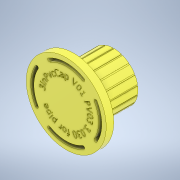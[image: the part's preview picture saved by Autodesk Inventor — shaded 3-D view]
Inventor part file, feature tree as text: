
AUTODESK INVENTOR PART (.ipt)
format: ipt  version: 2022.2 (Build 262287000, 287)  size: 949,760 bytes
history: native  units: in
note: dims shown in document units (in); Inventor stores cm internally (conversion verified against a paired STEP export)
features: extrude x6, sketch x6, pattern_circular x2, emboss x1
ambient origin geometry x8: Origin, YZ Plane, XZ Plane, XY Plane, X Axis, Y Axis, Z Axis, Center Point
bodies: Body1 (feature_tree)
feature tree (15):
  extrude  "Extrusion2"  Depth=0.4724in TaperAngle=0.0deg
  extrude  "Extrusion3"  Depth=2.5in TaperAngle=0.0deg
  extrude  "Extrusion7"  Depth=2.25in
  pattern_circular  "Circular Pattern1"  Angle=60.0deg  [1 undecoded]
  extrude  "Extrusion9"  Depth=0.201in
  pattern_circular  "Circular Pattern2"  [2 undecoded]
  sketch  "Sketch9"  dims[d17=0.315in d18=0.0in]
  extrude  "Extrusion10"  Depth=1.5748in TaperAngle=360.0deg
  emboss  "Emboss1"
  extrude  "Extrusion6"  Depth=0.04in
  sketch  "Sketch3"  dims[d1=3.03in d5=0.4724in d6=0.0in]
  sketch  "Sketch6"  dims[d7=0.25in d8=2.5in d9=0.0in]
  sketch  "Sketch8"  dims[d11=2.3944in d12=2.25in]
  sketch  "Sketch10"  dims[d26=2.125in]
  sketch  "Sketch11"  dims[d27=60.0deg d28=60.0deg d29=0.201in d30=0.0in d31=0.0in d32=1.5748in d33=360.0deg d35=0.04in d36=0.04in d39=1.0in d40=0.0in d41=7.0866in d42=360.0deg d45=5.0in d46=0.315in d47=0.315in d48=0.4724in d49=0.0in d50=3.0in d51=0.075in d52=0.0in]
note: 3 required parameter values undecoded (feature->parameter linkage not recoverable at this tier; creation-order binding heuristic only, values carry confidence <= 0.55)
